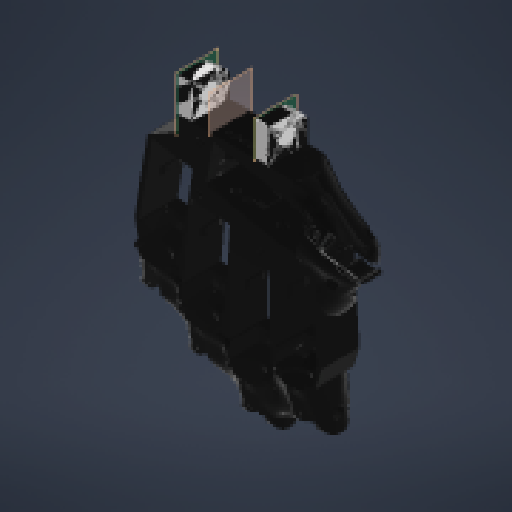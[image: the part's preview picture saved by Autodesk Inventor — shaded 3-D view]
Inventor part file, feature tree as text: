
AUTODESK INVENTOR PART (.ipt)
format: ipt  version: 2024 (Build 280153000, 153)  size: 953,856 bytes
history: native  units: in
note: dims shown in document units (in); Inventor stores cm internally (conversion verified against a paired STEP export)
features: plane x3, other x2, sketch x2, extrude x2, projected_geometry x1
ambient origin geometry x8: Origin, YZ Plane, XZ Plane, XY Plane, X Axis, Y Axis, Z Axis, Center Point
bodies: Body1 (feature_tree)
feature tree (10):
  other  "i2_WristLargeV2"
  sketch  "Sketch2"  dims[d4=0.0in d5=0.0in d6=0.2756in d7=0.0in]
  sketch  "Sketch3"  dims[d8=0.3937in d9=0.0in d10=0.3937in]
  plane  "Work Plane1"
  plane  "Work Plane2"
  extrude  "Extrusion3"  Depth=0.2756in TaperAngle=0.0deg
  extrude  "Extrusion4"  Depth=0.3937in
  plane  "Work Plane3"
  projected_geometry  "Projected Loop1"
  other  "MeshFeature1"
